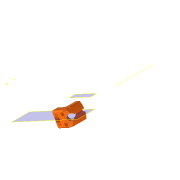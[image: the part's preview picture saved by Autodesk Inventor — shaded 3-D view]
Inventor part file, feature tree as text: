
AUTODESK INVENTOR PART (.ipt)
format: ipt  version: 2022.5 (Build 265521000, 521)  size: 467,456 bytes
history: native  units: in
note: dims shown in document units (in); Inventor stores cm internally (conversion verified against a paired STEP export)
features: extrude x9, other x8, sketch x8, reference x8, projected_geometry x3, plane x2, fillet x2, hole x2
ambient origin geometry x8: Origin, YZ Plane, XZ Plane, XY Plane, X Axis, Y Axis, Z Axis, Center Point
bodies: Solid1 (feature_tree)
feature tree (42):
  plane  "Work Plane1"
  extrude  "Extrusion1"  Depth=1.1811in
  plane  "Arbeitsebene3"
  other  "Arbeitsachse1"
  extrude  "Extrusion17"  TaperAngle=135.0deg  [1 undecoded]
  fillet  "Rundung4"  Radius=0.1575in
  hole  "Bohrung1"  [1 undecoded]
  extrude  "Extrusion19"  Depth=0.0591in
  hole  "Bohrung2"  [1 undecoded]
  extrude  "Extrusion20"  Depth=0.1181in
  extrude  "Extrusion21"  Depth=1.1811in
  extrude  "Extrusion22"  TaperAngle=0.0deg  [1 undecoded]
  fillet  "Rundung6"  Radius=0.4921in
  extrude  "Extrusion23"  Depth=0.1575in
  extrude  "Extrusion24"  TaperAngle=0.0deg  [1 undecoded]
  extrude  "Extrusion25"  Depth=0.3937in TaperAngle=0.0deg
  sketch  "Sketch1"  dims[d0=1.1811in d1=0.0in d22=0.5307in]
  reference  "Reference1"
  reference  "Referenz6"
  reference  "Referenz7"
  reference  "Referenz8"
  sketch  "Skizze22"  dims[d23=0.2653in d25=135.0deg d26=0.1575in]
  projected_geometry  "Projizierte Kontur13"
  projected_geometry  "Projizierte Kontur14"
  sketch  "Skizze24"  dims[d27=0.2362in d29=0.3937in]
  reference  "Referenz9"
  reference  "Referenz10"
  sketch  "Skizze25"  dims[d31=0.5906in d40=0.0591in]
  sketch  "Skizze26"  dims[d42=1.378in d70=0.4724in]
  reference  "Referenz11"
  reference  "Referenz12"
  sketch  "Skizze28"  dims[d71=0.0in d72=-0.0069in d73=0.1181in]
  projected_geometry  "Projizierte Kontur15"
  sketch  "Skizze29"  dims[d74=0.126in d75=0.2362in d76=0.2756in d77=1.1811in d78=90.0deg d79=0.315in d80=0.8108in d84=0.1102in]
  sketch  "Skizze30"  dims[d85=0.1102in d86=0.0in d87=0.0in d88=0.4921in d89=0.4921in d90=0.2362in d91=0.1575in d92=0.0787in d93=90.0deg d94=0.5118in d95=0.8108in d96=0.1575in d97=0.0in d98=0.0in d100=0.3937in d101=0.0in d102=0.0in d103=0.0in d104=0.1575in d105=0.6299in d106=0.6299in d107=0.1181in d108=0.1102in d109=0.1102in d110=0.0in d111=0.0in d112=45.0deg d113=0.0in d114=0.0in d115=0.1102in d116=0.1102in d117=0.3937in d118=0.0in]
  other  "<userpath>\Documents\Matchboxscope\INVENTOR\Matchboxscope_v0.iam"
  other  "Matchboxscope_v0.iam"
  other  "Matchboxscope_sample_v0:1"
  other  "Assembly_Matchboxscope_injectionmolded.iam"
  other  "IM_Matchboxscope_base_old:1"
  other  "IM_Matchboxscope_plate:2"
  other  "DIN 912 - ersetzt durch DIN EN ISO 4762 M3 x 25:2"
note: 5 required parameter values undecoded (feature->parameter linkage not recoverable at this tier; creation-order binding heuristic only, values carry confidence <= 0.55)
